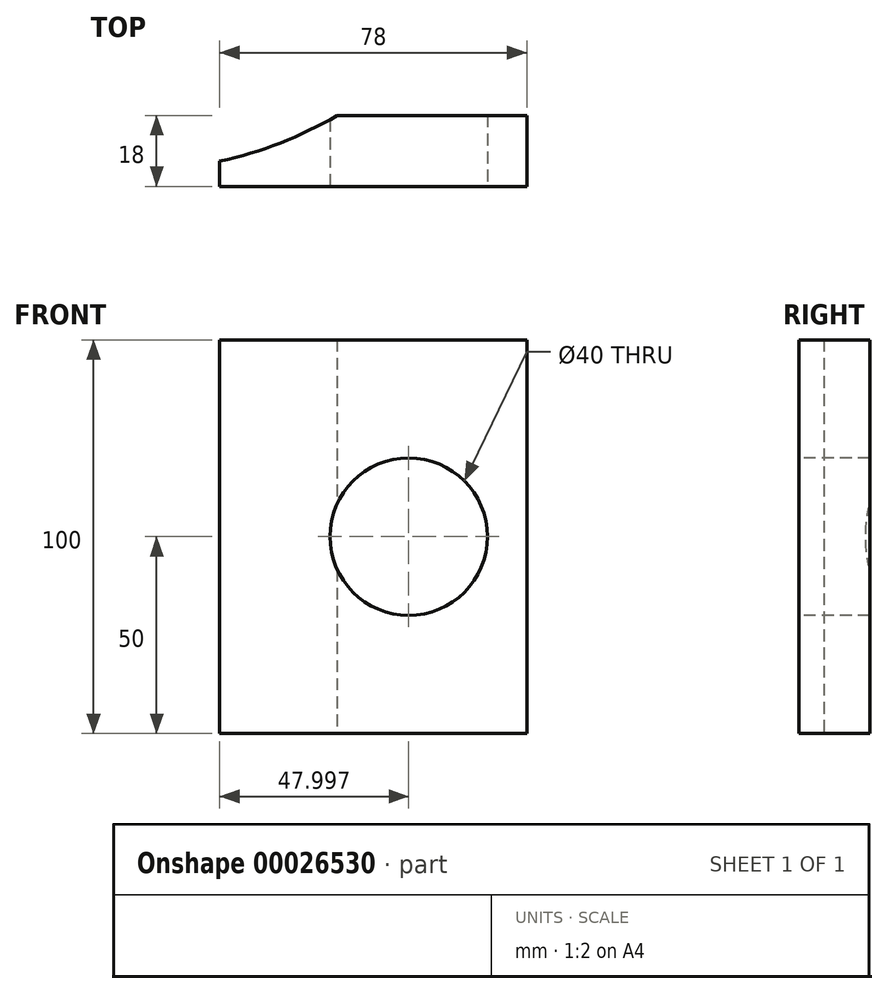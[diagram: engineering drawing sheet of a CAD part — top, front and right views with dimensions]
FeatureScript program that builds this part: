
annotation { "Feature Type Name" : "Feature", "Feature Type Description" : "" }
export const myFeature = defineFeature(function(context is Context, id is Id, definition is map)
    precondition{}
    {
        {
            var Q0;
            Q0=qCreatedBy(makeId("Top.planeOp"),FACE);
            var sketch = newSketch(context, id + "F0", { "sketchPlane" : qUnion([Q0])});
            skArc(sketch, "E0", {"start": v(34.96, 91.8) * mm, "mid": v(-134.14, 76.3) * mm, "end": v(-20.7, -50.05) * mm});
            skArc(sketch, "E1", {"start": v(54.3, 41.6) * mm, "mid": v(-129.12, 96.76) * mm, "end": v(-6.54, -50.41) * mm});
            skLineSegment(sketch, "E2", {"start": v(57.3, 41.6) * mm, "end": v(57.3, -83.4) * mm});
            skLineSegment(sketch, "E3", {"start": v(54.3, 41.6) * mm, "end": v(54.3, -65.4) * mm});
            skLineSegment(sketch, "E4", {"start": v(-23.7, -59.02) * mm, "end": v(-23.7, -83.4) * mm});
            skLineSegment(sketch, "E5", {"start": v(57.3, -65.4) * mm, "end": v(-23.7, -65.4) * mm});
            skLineSegment(sketch, "E6", {"start": v(79.3, 41.6) * mm, "end": v(79.19, -83.4) * mm});
            skLineSegment(sketch, "E7", {"start": v(-12.85, -33.67) * mm, "end": v(-13.26, -32.74) * mm});
            skLineSegment(sketch, "E8", {"start": v(28.64, 74.05) * mm, "end": v(29.57, 74.45) * mm});
            skArc(sketch, "E9", {"start": v(13.66, 78.69) * mm, "mid": v(-110.87, 67.17) * mm, "end": v(-27.4, -25.96) * mm});
            skPoint(sketch, "E10.visualSharp", {"position": v(41.37, 79.6) * mm});
            skArc(sketch, "E10.filletArc", {"start": v(29.57, 74.45) * mm, "mid": v(36.23, 81.9) * mm, "end": v(34.96, 91.8) * mm});
            skPoint(sketch, "E11.visualSharp", {"position": v(18.45, 69.6) * mm});
            skArc(sketch, "E11.filletArc", {"start": v(13.66, 78.69) * mm, "mid": v(20.3, 73.59) * mm, "end": v(28.64, 74.05) * mm});
            skPoint(sketch, "E12.visualSharp", {"position": v(-17.7, -22.55) * mm});
            skArc(sketch, "E12.filletArc", {"start": v(-13.26, -32.74) * mm, "mid": v(-19.06, -26.72) * mm, "end": v(-27.4, -25.96) * mm});
            skPoint(sketch, "E13.visualSharp", {"position": v(-7.7, -45.47) * mm});
            skArc(sketch, "E13.filletArc", {"start": v(-20.7, -50.05) * mm, "mid": v(-13.03, -43.65) * mm, "end": v(-12.85, -33.67) * mm});
            skLineSegment(sketch, "E14", {"start": v(-5.7, -53.31) * mm, "end": v(-6.54, -50.41) * mm});
            skArc(sketch, "E15", {"start": v(79.3, 41.38) * mm, "mid": v(-134.01, 130.07) * mm, "end": v(-45.7, -83.4) * mm});
            skLineSegment(sketch, "E16", {"start": v(-45.7, -83.4) * mm, "end": v(-23.7, -83.4) * mm});
            skLineSegment(sketch, "E17", {"start": v(-23.7, -83.4) * mm, "end": v(79.19, -83.4) * mm});
            skLineSegment(sketch, "E18", {"start": v(54.3, -47.4) * mm, "end": v(6.14, -47.4) * mm});
            skCircle(sketch, "E19", {"center": v(-45.7, 41.6) * mm, "radius": 103 * mm});
            skSolve(sketch);
        }
        {
            var Q0;
            {var subQ1=sQuery(id+"F0.wireOp",EDGE,"E18");Q0=makeQuery(id+"F0.imprint","IMPRINT",FACE,{"disambiguationData":[TD([[makeQuery(id+"F0.imprint","IMPRINT",EDGE,{"derivedFrom":subQ1}),1.0]])]});}
            extrude(context, id + "F1", {"entities" : qUnion([Q0]), "depth" : 100 * mm});
        }
        {
            var Q0;
            Q0=makeQuery(id+"F1.opExtrude","SWEPT_FACE",FACE,{"disambiguationData":[OSD([sQuery(id+"F0.wireOp",EDGE,"E5")])]});
            var sketch = newSketch(context, id + "F2", { "sketchPlane" : qUnion([Q0])});
            skCircle(sketch, "E20", {"center": v(24.3, 50) * mm, "radius": 20 * mm});
            skSolve(sketch);
        }
        {
            var Q0;
            Q0=makeQuery(id+"F2.imprint","IMPRINT",FACE,{"disambiguationData":[TD([[makeQuery(id+"F2.imprint","IMPRINT",EDGE,{"derivedFrom":sQuery(id+"F2.wireOp",EDGE,"E20")}),1.0]])]});
            extrude(context, id + "F3", {"entities" : qUnion([Q0]), "operationType" : NewBodyOperationType.REMOVE, "oppositeDirection" : true, "depth" : 25 * mm});
        }
    });
